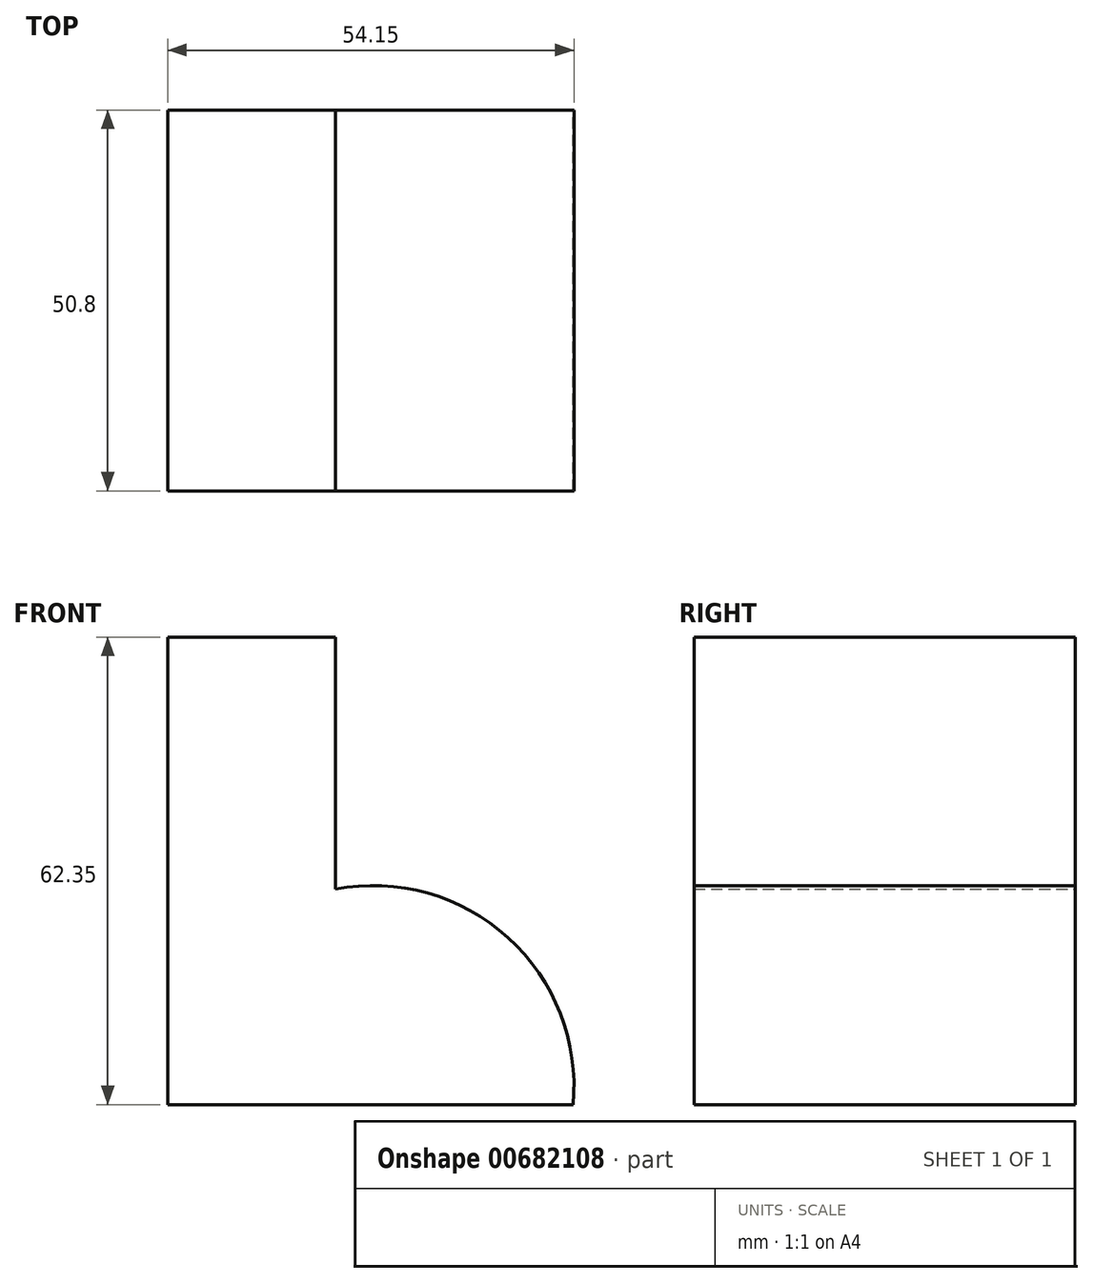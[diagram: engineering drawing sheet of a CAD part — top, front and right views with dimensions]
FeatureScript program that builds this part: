
annotation { "Feature Type Name" : "Feature", "Feature Type Description" : "" }
export const myFeature = defineFeature(function(context is Context, id is Id, definition is map)
    precondition{}
    {
        {
            var Q0;
            Q0=qCreatedBy(makeId("Front.planeOp"),FACE);
            var sketch = newSketch(context, id + "F0", { "sketchPlane" : qUnion([Q0])});
            skLineSegment(sketch, "E0", {"start": v(-62.54, 62.35) * mm, "end": v(-62.54, 0) * mm});
            skLineSegment(sketch, "E1", {"start": v(-62.54, 0) * mm, "end": v(-8.5, 0) * mm});
            skLineSegment(sketch, "E2", {"start": v(-40.2, 62.35) * mm, "end": v(-62.54, 62.35) * mm});
            skLineSegment(sketch, "E3", {"start": v(-40.2, 62.35) * mm, "end": v(-40.2, 28.74) * mm});
            skArc(sketch, "E4", {"start": v(-8.5, 0) * mm, "mid": v(-17.18, 22.27) * mm, "end": v(-40.2, 28.74) * mm});
            skSolve(sketch);
        }
        {
            var Q0;
            Q0 = qSketchRegion(id + "F0", true);
            extrude(context, id + "F1", {"entities" : qUnion([Q0]), "depth" : 50.8 * mm, "offsetDistance" : 25.4 * mm});
        }
    });
